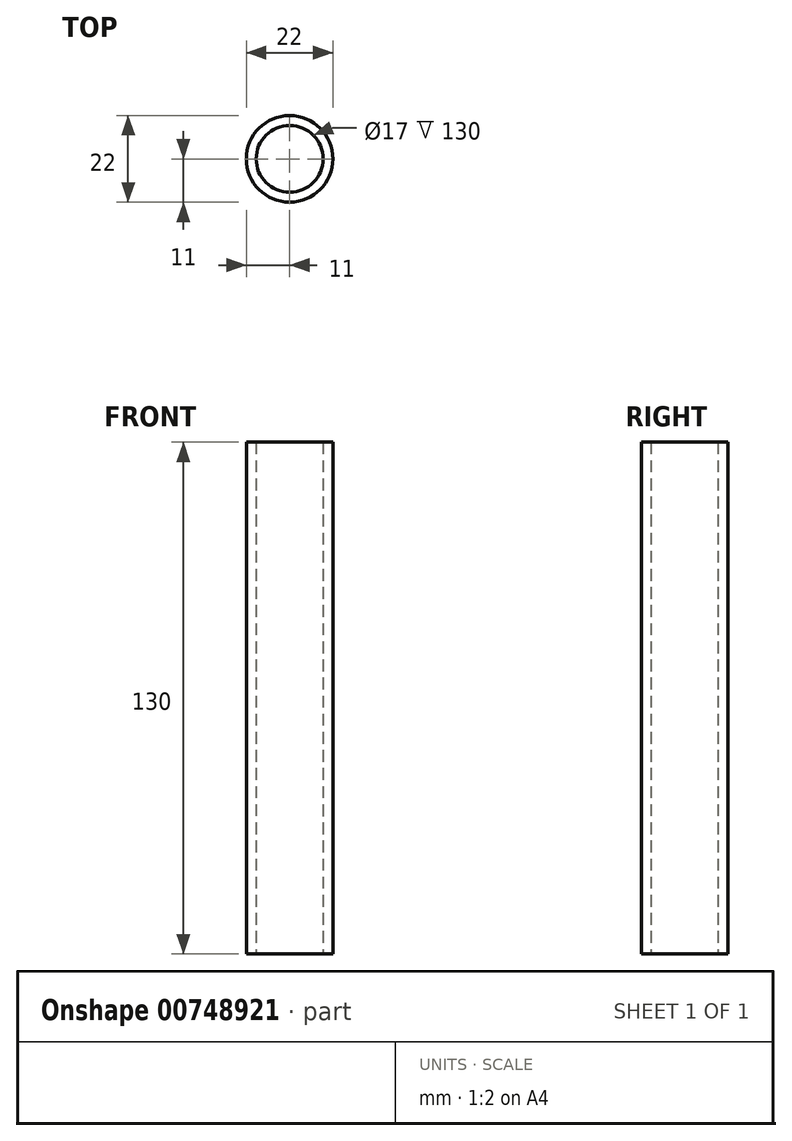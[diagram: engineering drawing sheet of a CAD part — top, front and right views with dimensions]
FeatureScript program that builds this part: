
annotation { "Feature Type Name" : "Feature", "Feature Type Description" : "" }
export const myFeature = defineFeature(function(context is Context, id is Id, definition is map)
    precondition{}
    {
        {
            var Q0;
            Q0=qCreatedBy(makeId("Top.planeOp"), FACE);
            var sketch = newSketch(context, id + "F0", { "sketchPlane" : qUnion([Q0])});
            skCircle(sketch, "E0", {"center": v(0, 0) * mm, "radius": 11 * mm});
            skCircle(sketch, "E1", {"center": v(0, 0) * mm, "radius": 8.5 * mm});
            skSolve(sketch);
        }
        {
            var Q0;
            Q0 = qSketchRegion(id + "F0", true);
            extrude(context, id + "F1", {"entities" : qUnion([Q0]), "depth" : 130 * mm, "offsetDistance" : 25 * mm, "symmetric" : true});
        }
    });
